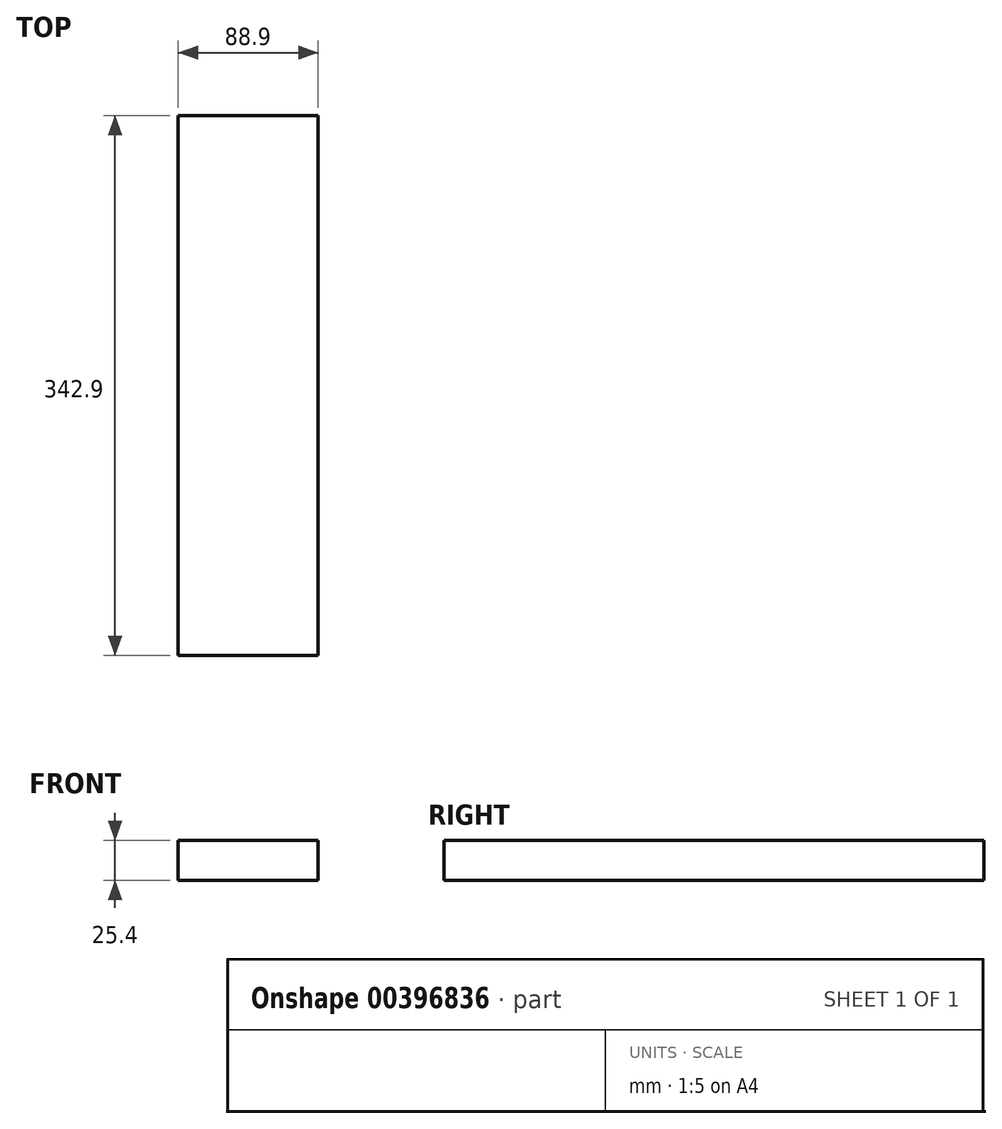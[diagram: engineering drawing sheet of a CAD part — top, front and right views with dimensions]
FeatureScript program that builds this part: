
annotation { "Feature Type Name" : "Feature", "Feature Type Description" : "" }
export const myFeature = defineFeature(function(context is Context, id is Id, definition is map)
    precondition{}
    {
        {
            var Q0;
            Q0=qCreatedBy(makeId("Top.planeOp"),FACE);
            var sketch = newSketch(context, id + "F0", { "sketchPlane" : qUnion([Q0])});
            skLineSegment(sketch, "E0.bottom", {"start": v(-39.16, 171.45) * mm, "end": v(49.74, 171.45) * mm});
            skLineSegment(sketch, "E0.top", {"start": v(-39.16, -171.45) * mm, "end": v(49.74, -171.45) * mm});
            skLineSegment(sketch, "E0.left", {"start": v(-39.16, 171.45) * mm, "end": v(-39.16, -171.45) * mm});
            skLineSegment(sketch, "E0.right", {"start": v(49.74, 171.45) * mm, "end": v(49.74, -171.45) * mm});
            skPoint(sketch, "E0.middle", {"position": v(5.29, 0) * mm});
            skSolve(sketch);
        }
        {
            var Q0;
            Q0=makeQuery(id+"F0.imprint","IMPRINT",FACE,{"disambiguationData":[TD([[makeQuery(id+"F0.imprint","IMPRINT",EDGE,{"derivedFrom":sQuery(id+"F0.wireOp",EDGE,"E0.bottom")}),-1.0]])]});
            extrude(context, id + "F1", {"entities" : qUnion([Q0]), "depth" : 25.4 * mm});
        }
    });
